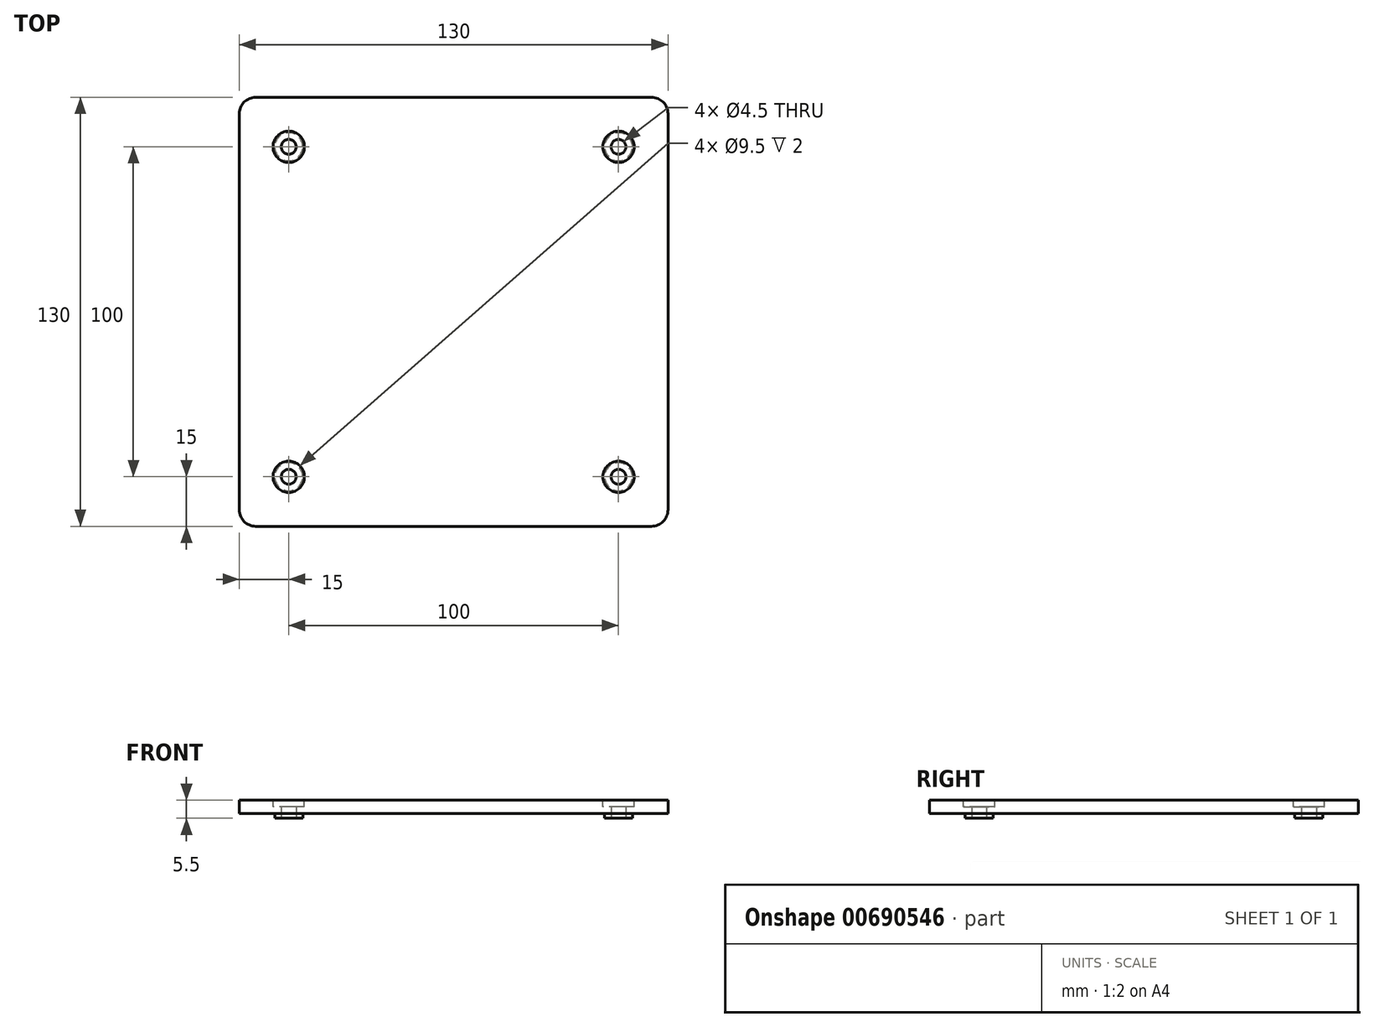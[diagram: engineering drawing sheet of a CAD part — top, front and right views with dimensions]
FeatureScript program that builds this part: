
annotation { "Feature Type Name" : "Feature", "Feature Type Description" : "" }
export const myFeature = defineFeature(function(context is Context, id is Id, definition is map)
    precondition{}
    {
        {
            var Q0;
            Q0=qCreatedBy(makeId("Top.planeOp"),FACE);
            var sketch = newSketch(context, id + "F0", { "sketchPlane" : qUnion([Q0])});
            skLineSegment(sketch, "E0.bottom", {"start": v(-60, -65) * mm, "end": v(60, -65) * mm});
            skLineSegment(sketch, "E0.top", {"start": v(-60, 65) * mm, "end": v(60, 65) * mm});
            skLineSegment(sketch, "E0.left", {"start": v(-65, -60) * mm, "end": v(-65, 60) * mm});
            skLineSegment(sketch, "E0.right", {"start": v(65, -60) * mm, "end": v(65, 60) * mm});
            skPoint(sketch, "E0.middle", {"position": v(0, 0) * mm});
            skLineSegment(sketch, "E1.0", {"start": v(-50, 50) * mm, "end": v(50, 50) * mm, "construction": true});
            skLineSegment(sketch, "E1.1", {"start": v(-50, -50) * mm, "end": v(-50, 50) * mm, "construction": true});
            skLineSegment(sketch, "E1.2", {"start": v(-50, -50) * mm, "end": v(50, -50) * mm, "construction": true});
            skLineSegment(sketch, "E1.3", {"start": v(50, -50) * mm, "end": v(50, 50) * mm, "construction": true});
            skCircle(sketch, "E2", {"center": v(-50, 50) * mm, "radius": 2.25 * mm});
            skCircle(sketch, "E3", {"center": v(-50, 50) * mm, "radius": 4.25 * mm});
            skCircle(sketch, "E4", {"center": v(50, 50) * mm, "radius": 2.25 * mm});
            skCircle(sketch, "E5", {"center": v(50, 50) * mm, "radius": 4.25 * mm});
            skCircle(sketch, "E6", {"center": v(-50, -50) * mm, "radius": 2.25 * mm});
            skCircle(sketch, "E7", {"center": v(-50, -50) * mm, "radius": 4.25 * mm});
            skCircle(sketch, "E8", {"center": v(50, -50) * mm, "radius": 2.25 * mm});
            skCircle(sketch, "E9", {"center": v(50, -50) * mm, "radius": 4.25 * mm});
            skPoint(sketch, "E10.visualSharp", {"position": v(-65, 65) * mm});
            skArc(sketch, "E10.filletArc", {"start": v(-60, 65) * mm, "mid": v(-63.54, 63.54) * mm, "end": v(-65, 60) * mm});
            skPoint(sketch, "E11.visualSharp", {"position": v(65, 65) * mm});
            skArc(sketch, "E11.filletArc", {"start": v(65, 60) * mm, "mid": v(63.54, 63.54) * mm, "end": v(60, 65) * mm});
            skPoint(sketch, "E12.visualSharp", {"position": v(65, -65) * mm});
            skArc(sketch, "E12.filletArc", {"start": v(60, -65) * mm, "mid": v(63.54, -63.54) * mm, "end": v(65, -60) * mm});
            skPoint(sketch, "E13.visualSharp", {"position": v(-65, -65) * mm});
            skArc(sketch, "E13.filletArc", {"start": v(-65, -60) * mm, "mid": v(-63.54, -63.54) * mm, "end": v(-60, -65) * mm});
            skSolve(sketch);
        }
        {
            var Q0;
            Q0=makeQuery(id+"F0.imprint","IMPRINT",FACE,{"disambiguationData":[TD([[makeQuery(id+"F0.imprint","IMPRINT",EDGE,{"derivedFrom":sQuery(id+"F0.wireOp",EDGE,"E6")}),-1.0]])]});
            var Q1;
            Q1=makeQuery(id+"F0.imprint","IMPRINT",FACE,{"disambiguationData":[TD([[makeQuery(id+"F0.imprint","IMPRINT",EDGE,{"derivedFrom":sQuery(id+"F0.wireOp",EDGE,"E8")}),-1.0]])]});
            var Q2;
            Q2=makeQuery(id+"F0.imprint","IMPRINT",FACE,{"disambiguationData":[TD([[makeQuery(id+"F0.imprint","IMPRINT",EDGE,{"derivedFrom":sQuery(id+"F0.wireOp",EDGE,"E4")}),-1.0]])]});
            var Q3;
            Q3=makeQuery(id+"F0.imprint","IMPRINT",FACE,{"disambiguationData":[TD([[makeQuery(id+"F0.imprint","IMPRINT",EDGE,{"derivedFrom":sQuery(id+"F0.wireOp",EDGE,"E2")}),-1.0]])]});
            var Q4;
            Q4=makeQuery(id+"F0.imprint","IMPRINT",FACE,{"disambiguationData":[TD([[makeQuery(id+"F0.imprint","IMPRINT",EDGE,{"derivedFrom":sQuery(id+"F0.wireOp",EDGE,"E0.bottom")}),1.0]])]});
            extrude(context, id + "F1", {"entities" : qUnion([Q0, Q1, Q2, Q3, Q4]), "depth" : 4 * mm, "offsetDistance" : 25 * mm});
        }
        {
            var Q0;
            Q0=makeQuery(id+"F0.imprint","IMPRINT",FACE,{"disambiguationData":[TD([[makeQuery(id+"F0.imprint","IMPRINT",EDGE,{"derivedFrom":sQuery(id+"F0.wireOp",EDGE,"E8")}),-1.0]])]});
            var Q1;
            Q1=makeQuery(id+"F0.imprint","IMPRINT",FACE,{"disambiguationData":[TD([[makeQuery(id+"F0.imprint","IMPRINT",EDGE,{"derivedFrom":sQuery(id+"F0.wireOp",EDGE,"E4")}),-1.0]])]});
            var Q2;
            Q2=makeQuery(id+"F0.imprint","IMPRINT",FACE,{"disambiguationData":[TD([[makeQuery(id+"F0.imprint","IMPRINT",EDGE,{"derivedFrom":sQuery(id+"F0.wireOp",EDGE,"E2")}),-1.0]])]});
            var Q3;
            Q3=makeQuery(id+"F0.imprint","IMPRINT",FACE,{"disambiguationData":[TD([[makeQuery(id+"F0.imprint","IMPRINT",EDGE,{"derivedFrom":sQuery(id+"F0.wireOp",EDGE,"E6")}),-1.0]])]});
            extrude(context, id + "F2", {"entities" : qUnion([Q0, Q1, Q2, Q3]), "operationType" : NewBodyOperationType.ADD, "oppositeDirection" : true, "depth" : 1.5 * mm, "offsetDistance" : 25 * mm});
        }
        {
            var Q0;
            Q0=makeQuery(id+"F1.opExtrude","CAP_FACE",FACE,{"disambiguationData":[OSD([sQuery(id+"F0.wireOp",EDGE,"E0.bottom"),sQuery(id+"F0.wireOp",EDGE,"E0.top"),sQuery(id+"F0.wireOp",EDGE,"E0.left"),sQuery(id+"F0.wireOp",EDGE,"E0.right"),sQuery(id+"F0.wireOp",EDGE,"E2"),sQuery(id+"F0.wireOp",EDGE,"E4"),sQuery(id+"F0.wireOp",EDGE,"E6"),sQuery(id+"F0.wireOp",EDGE,"E8"),sQuery(id+"F0.wireOp",EDGE,"E10.filletArc"),sQuery(id+"F0.wireOp",EDGE,"E11.filletArc"),sQuery(id+"F0.wireOp",EDGE,"E12.filletArc"),sQuery(id+"F0.wireOp",EDGE,"E13.filletArc")])],"isStart":false});
            var sketch = newSketch(context, id + "F3", { "sketchPlane" : qUnion([Q0])});
            skCircle(sketch, "E14", {"center": v(-50, -50) * mm, "radius": 4.75 * mm});
            skCircle(sketch, "E15", {"center": v(50, -50) * mm, "radius": 4.75 * mm});
            skCircle(sketch, "E16", {"center": v(50, 50) * mm, "radius": 4.75 * mm});
            skCircle(sketch, "E17", {"center": v(-50, 50) * mm, "radius": 4.75 * mm});
            skSolve(sketch);
        }
        {
            var Q0;
            Q0=makeQuery(id+"F3.imprint","IMPRINT",FACE,{"disambiguationData":[TD([[makeQuery(id+"F3.imprint","IMPRINT",EDGE,{"derivedFrom":sQuery(id+"F3.wireOp",EDGE,"E17")}),1.0]])]});
            var Q1;
            Q1=makeQuery(id+"F3.imprint","IMPRINT",FACE,{"disambiguationData":[TD([[makeQuery(id+"F3.imprint","IMPRINT",EDGE,{"derivedFrom":sQuery(id+"F3.wireOp",EDGE,"E16")}),1.0]])]});
            var Q2;
            Q2=makeQuery(id+"F3.imprint","IMPRINT",FACE,{"disambiguationData":[TD([[makeQuery(id+"F3.imprint","IMPRINT",EDGE,{"derivedFrom":sQuery(id+"F3.wireOp",EDGE,"E15")}),1.0]])]});
            var Q3;
            Q3=makeQuery(id+"F3.imprint","IMPRINT",FACE,{"disambiguationData":[TD([[makeQuery(id+"F3.imprint","IMPRINT",EDGE,{"derivedFrom":sQuery(id+"F3.wireOp",EDGE,"E14")}),1.0]])]});
            extrude(context, id + "F4", {"entities" : qUnion([Q0, Q1, Q2, Q3]), "operationType" : NewBodyOperationType.REMOVE, "oppositeDirection" : true, "depth" : 2 * mm, "offsetDistance" : 25 * mm});
        }
    });
